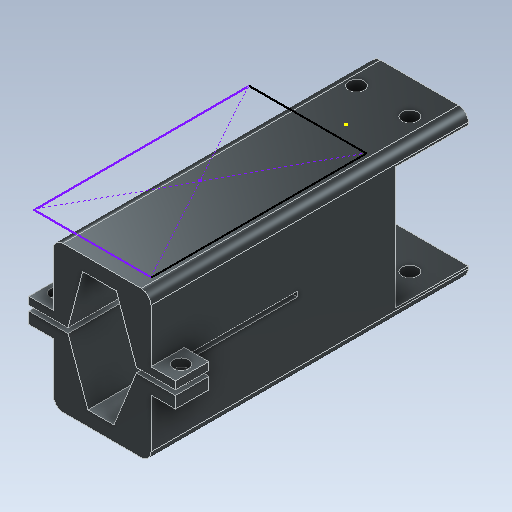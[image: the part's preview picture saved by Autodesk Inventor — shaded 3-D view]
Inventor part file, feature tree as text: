
AUTODESK INVENTOR PART (.ipt)
format: ipt  version: 2021 (Build 250183000, 183)  size: 248,320 bytes
history: native  units: mm
features: sketch x10, extrude x8, other x4, fillet x2, reference x2, shell x1, mirror x1
ambient origin geometry x8: Origin, YZ Plane, XZ Plane, XY Plane, X Axis, Y Axis, Z Axis, Center Point
bodies: Solid1 (feature_tree)
feature tree (28):
  extrude  "Extrusion1"  Depth=30.0mm
  shell  "Shell1"  Thickness=50.0mm
  sketch  "Sketch2"  dims[d4=3.0mm d5=2.5mm]
  extrude  "Extrusion2"  Depth=2.5mm
  sketch  "Sketch4"  dims[d16=2.0mm d17=5.0mm]
  extrude  "Extrusion4"  Depth=15.0mm TaperAngle=0.0deg
  fillet  "Fillet1"  [1 undecoded]
  fillet  "Fillet2"  Radius=2.0mm
  extrude  "Extrusion5"  Depth=5.0mm
  extrude  "Extrusion6"  Depth=1.0mm
  extrude  "Extrusion7"  Depth=30.0mm TaperAngle=0.0deg
  extrude  "Extrusion8"  Depth=5.0mm TaperAngle=0.0deg
  extrude  "Extrusion9"  [1 undecoded]
  mirror  "Mirror1"
  sketch  "Sketch1"  dims[d0=20.0mm d1=30.0mm d2=50.0mm d3=0.0mm]
  sketch  "Sketch3"  dims[d6=2.5mm d7=15.0mm d8=0.0mm d13=0.0mm d14=0.0mm d15=2.0mm]
  sketch  "Sketch6"  dims[d18=10.0mm d19=0.0mm d20=1.0mm]
  reference  "Reference1"
  reference  "Reference2"
  sketch  "Sketch7"  dims[d21=30.0mm d22=0.0mm d23=30.0mm d24=0.0mm]
  sketch  "Sketch8"  dims[d25=5.0mm d26=0.0mm d27=6.25mm d28=0.0mm]
  sketch  "Sketch9"
  sketch  "Sketch10"
  sketch  "Sketch11"
  parser-record x1  (decoder bookkeeping rows leaked as tree rows — omitted from the tree; the rows remain in map.json)
  other  "whole_assembly.iam"
  other  "tool_holder:1"
  other  "Part3:1"
note: 2 required parameter values undecoded (feature->parameter linkage not recoverable at this tier; creation-order binding heuristic only, values carry confidence <= 0.55)
note: 1 file-system path scrubbed to <path> (originals preserved in map.json)
